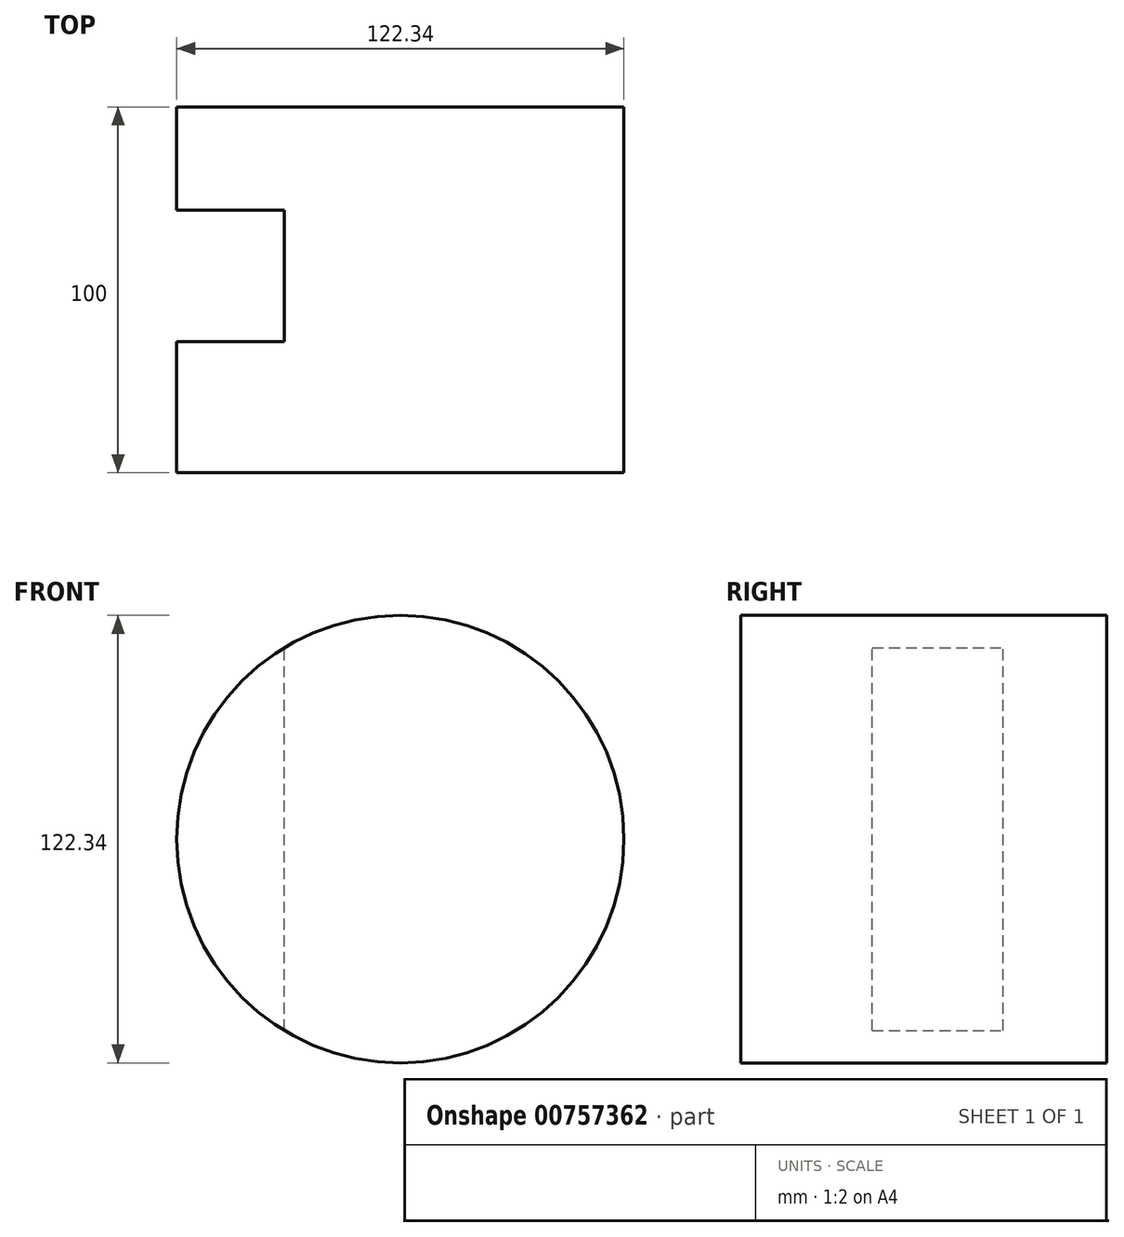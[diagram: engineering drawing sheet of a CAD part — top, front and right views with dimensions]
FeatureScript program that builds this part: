
annotation { "Feature Type Name" : "Feature", "Feature Type Description" : "" }
export const myFeature = defineFeature(function(context is Context, id is Id, definition is map)
    precondition{}
    {
        {
            var Q0;
            Q0=qCreatedBy(makeId("Front.planeOp"),FACE);
            var sketch = newSketch(context, id + "F0", { "sketchPlane" : qUnion([Q0])});
            skCircle(sketch, "E0", {"center": v(0, 0) * mm, "radius": 61.17 * mm});
            skSolve(sketch);
        }
        {
            var Q0;
            Q0 = qSketchRegion(id + "F0", true);
            extrude(context, id + "F1", {"entities" : qUnion([Q0]), "depth" : 100 * mm, "offsetDistance" : 25.4 * mm});
        }
        {
            var Q0;
            Q0=qCreatedBy(makeId("Top.planeOp"),FACE);
            var sketch = newSketch(context, id + "F2", { "sketchPlane" : qUnion([Q0])});
            skLineSegment(sketch, "E1.bottom", {"start": v(-31.7, -64.1) * mm, "end": v(-70.51, -64.1) * mm});
            skLineSegment(sketch, "E1.top", {"start": v(-31.7, -28.27) * mm, "end": v(-70.51, -28.27) * mm});
            skLineSegment(sketch, "E1.left", {"start": v(-31.7, -64.1) * mm, "end": v(-31.7, -28.27) * mm});
            skLineSegment(sketch, "E1.right", {"start": v(-70.51, -64.1) * mm, "end": v(-70.51, -28.27) * mm});
            skPoint(sketch, "E1.middle", {"position": v(-51.1, -46.18) * mm});
            skSolve(sketch);
        }
        {
            var Q0;
            Q0 = qSketchRegion(id + "F2", true);
            extrude(context, id + "F3", {"entities" : qUnion([Q0]), "operationType" : NewBodyOperationType.REMOVE, "endBound" : BoundingType.SYMMETRIC, "oppositeDirection" : true, "depth" : 185.9 * mm, "offsetDistance" : 25.4 * mm});
        }
    });
